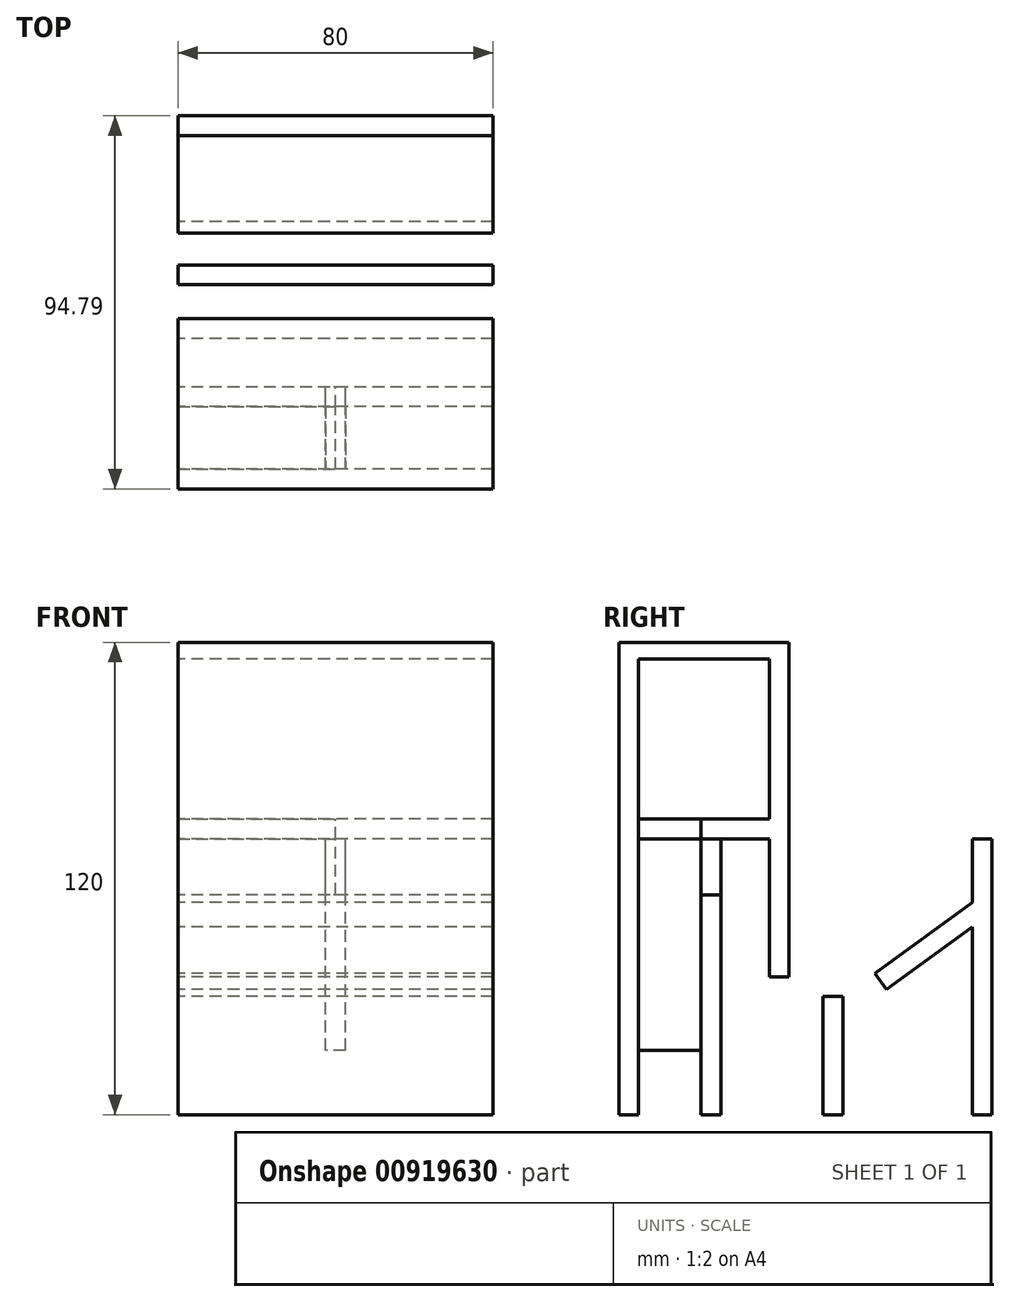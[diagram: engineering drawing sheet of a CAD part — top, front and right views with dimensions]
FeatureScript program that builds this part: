
annotation { "Feature Type Name" : "Feature", "Feature Type Description" : "" }
export const myFeature = defineFeature(function(context is Context, id is Id, definition is map)
    precondition{}
    {
        {
            var Q0;
            Q0=qCreatedBy(makeId("Right.planeOp"),FACE);
            var sketch = newSketch(context, id + "F0", { "sketchPlane" : qUnion([Q0])});
            skLineSegment(sketch, "E0.bottom", {"start": v(27.57, 0) * mm, "end": v(32.57, 0) * mm});
            skLineSegment(sketch, "E0.top", {"start": v(27.57, 30) * mm, "end": v(32.57, 30) * mm});
            skLineSegment(sketch, "E0.left", {"start": v(27.57, 0) * mm, "end": v(27.57, 30) * mm});
            skLineSegment(sketch, "E0.right", {"start": v(32.57, 0) * mm, "end": v(32.57, 30) * mm});
            skLineSegment(sketch, "E1", {"start": v(13.91, 35) * mm, "end": v(13.91, 70.09) * mm});
            skLineSegment(sketch, "E2", {"start": v(32.57, 30) * mm, "end": v(40.66, 35.88) * mm});
            skLineSegment(sketch, "E3", {"start": v(40.66, 35.88) * mm, "end": v(65.49, 53.92) * mm});
            skLineSegment(sketch, "E4", {"start": v(-19.3, 0) * mm, "end": v(-19.3, 70.09) * mm});
            skLineSegment(sketch, "E5", {"start": v(-19.3, 70.09) * mm, "end": v(13.91, 70.09) * mm});
            skLineSegment(sketch, "E6", {"start": v(32.57, 0) * mm, "end": v(65.49, 0) * mm});
            skLineSegment(sketch, "E7", {"start": v(65.49, 0) * mm, "end": v(65.49, 53.92) * mm});
            skLineSegment(sketch, "E8", {"start": v(-19.3, 70.09) * mm, "end": v(-19.3, 115.83) * mm});
            skLineSegment(sketch, "E9", {"start": v(-19.3, 115.83) * mm, "end": v(13.91, 115.83) * mm});
            skLineSegment(sketch, "E10.bottom", {"start": v(-19.3, 0) * mm, "end": v(-24.3, 0) * mm});
            skLineSegment(sketch, "E10.top", {"start": v(-19.3, 115.83) * mm, "end": v(-24.3, 115.83) * mm});
            skLineSegment(sketch, "E10.left", {"start": v(-19.3, 0) * mm, "end": v(-19.3, 115.83) * mm});
            skLineSegment(sketch, "E10.right", {"start": v(-24.3, 0) * mm, "end": v(-24.3, 115.83) * mm});
            skLineSegment(sketch, "E11.bottom", {"start": v(-24.3, 115.83) * mm, "end": v(13.91, 115.83) * mm});
            skLineSegment(sketch, "E11.top", {"start": v(-24.3, 120) * mm, "end": v(13.91, 120) * mm});
            skLineSegment(sketch, "E11.left", {"start": v(-24.3, 115.83) * mm, "end": v(-24.3, 120) * mm});
            skLineSegment(sketch, "E11.right", {"start": v(13.91, 115.83) * mm, "end": v(13.91, 120) * mm});
            skLineSegment(sketch, "E12.bottom", {"start": v(13.91, 120) * mm, "end": v(18.91, 120) * mm});
            skLineSegment(sketch, "E12.top", {"start": v(0, 70.09) * mm, "end": v(18.91, 70.09) * mm});
            skLineSegment(sketch, "E12.right", {"start": v(18.91, 120) * mm, "end": v(18.91, 70.09) * mm});
            skLineSegment(sketch, "E13", {"start": v(18.91, 70.09) * mm, "end": v(18.91, 35) * mm});
            skLineSegment(sketch, "E14", {"start": v(18.91, 35) * mm, "end": v(13.91, 35) * mm});
            skLineSegment(sketch, "E15", {"start": v(18.91, 35) * mm, "end": v(27.57, 30) * mm});
            skLineSegment(sketch, "E16", {"start": v(70.49, 53.94) * mm, "end": v(70.49, 0) * mm});
            skLineSegment(sketch, "E17", {"start": v(70.49, 0) * mm, "end": v(65.49, 0) * mm});
            skLineSegment(sketch, "E18", {"start": v(-19.3, 75.09) * mm, "end": v(13.91, 75.09) * mm});
            skLineSegment(sketch, "E19", {"start": v(13.91, 70.09) * mm, "end": v(13.91, 75.09) * mm});
            skLineSegment(sketch, "E20", {"start": v(13.91, 115.83) * mm, "end": v(13.91, 75.09) * mm});
            skLineSegment(sketch, "E21", {"start": v(40.66, 35.88) * mm, "end": v(43.6, 31.83) * mm});
            skLineSegment(sketch, "E22", {"start": v(43.6, 31.83) * mm, "end": v(65.49, 47.74) * mm});
            skLineSegment(sketch, "E23", {"start": v(-19.3, 0) * mm, "end": v(27.57, 0) * mm});
            skLineSegment(sketch, "E24", {"start": v(-3.45, 0) * mm, "end": v(-3.45, 55.88) * mm});
            skLineSegment(sketch, "E25", {"start": v(-3.45, 55.88) * mm, "end": v(1.55, 55.88) * mm});
            skLineSegment(sketch, "E26", {"start": v(1.55, 55.88) * mm, "end": v(1.55, 0) * mm});
            skLineSegment(sketch, "E27", {"start": v(65.49, 70.09) * mm, "end": v(65.49, 53.92) * mm});
            skLineSegment(sketch, "E28", {"start": v(65.49, 70.09) * mm, "end": v(70.49, 70.09) * mm});
            skLineSegment(sketch, "E29", {"start": v(70.49, 70.09) * mm, "end": v(70.49, 53.94) * mm});
            skLineSegment(sketch, "E30", {"start": v(-3.45, 55.88) * mm, "end": v(-3.45, 70.09) * mm});
            skLineSegment(sketch, "E31", {"start": v(1.55, 55.88) * mm, "end": v(1.55, 70.09) * mm});
            skLineSegment(sketch, "E32", {"start": v(-3.45, 70.09) * mm, "end": v(-3.45, 75.09) * mm});
            skLineSegment(sketch, "E33", {"start": v(-3.45, 16.34) * mm, "end": v(-19.3, 16.34) * mm});
            skSolve(sketch);
        }
        {
            var Q0;
            Q0=makeQuery(id+"F0.imprint","IMPRINT",FACE,{"disambiguationData":[TD([[makeQuery(id+"F0.imprint","IMPRINT",EDGE,{"derivedFrom":sQuery(id+"F0.wireOp",EDGE,"E11.top")}),-1.0]])]});
            var Q1;
            {var subQ5=sQuery(id+"F0.wireOp",EDGE,"E10.bottom");Q1=makeQuery(id+"F0.imprint","IMPRINT",FACE,{"disambiguationData":[TD([[makeQuery(id+"F0.imprint","IMPRINT",EDGE,{"derivedFrom":subQ5}),-1.0]])]});}
            var Q2;
            Q2=makeQuery(id+"F0.imprint","IMPRINT",FACE,{"disambiguationData":[TD([[makeQuery(id+"F0.imprint","IMPRINT",EDGE,{"derivedFrom":sQuery(id+"F0.wireOp",EDGE,"E11.right")}),-1.0]])]});
            var Q3;
            {var subQ0=sQuery(id+"F0.wireOp",EDGE,"E1");Q3=makeQuery(id+"F0.imprint","IMPRINT",FACE,{"disambiguationData":[TD([[makeQuery(id+"F0.imprint","IMPRINT",EDGE,{"derivedFrom":subQ0}),-1.0]])]});}
            var Q4;
            Q4=makeQuery(id+"F0.imprint","IMPRINT",FACE,{"disambiguationData":[TD([[makeQuery(id+"F0.imprint","IMPRINT",EDGE,{"derivedFrom":sQuery(id+"F0.wireOp",EDGE,"Fx7D5mdC-qbW7-CEck-KvEF-XUMli4D04gyy")}),1.0]])]});
            var Q5;
            Q5=makeQuery(id+"F0.imprint","IMPRINT",FACE,{"disambiguationData":[TD([[makeQuery(id+"F0.imprint","IMPRINT",EDGE,{"derivedFrom":sQuery(id+"F0.wireOp",EDGE,"E0.bottom")}),1.0]])]});
            var Q6;
            {var subQ0=sQuery(id+"F0.wireOp",EDGE,"E3");Q6=makeQuery(id+"F0.imprint","IMPRINT",FACE,{"disambiguationData":[TD([[makeQuery(id+"F0.imprint","IMPRINT",EDGE,{"derivedFrom":subQ0}),-1.0]])]});}
            var Q7;
            {var subQ0=sQuery(id+"F0.wireOp",EDGE,"xSf1LqSM-Zb7q-qxLd-u2kb-gej299T4ug9K");Q7=makeQuery(id+"F0.imprint","IMPRINT",FACE,{"disambiguationData":[TD([[makeQuery(id+"F0.imprint","IMPRINT",EDGE,{"derivedFrom":subQ0}),-1.0]])]});}
            var Q8;
            {var subQ0=sQuery(id+"F0.wireOp",EDGE,"E24");Q8=makeQuery(id+"F0.imprint","IMPRINT",FACE,{"disambiguationData":[TD([[makeQuery(id+"F0.imprint","IMPRINT",EDGE,{"derivedFrom":subQ0}),-1.0]])]});}
            var Q9;
            Q9=makeQuery(id+"F0.imprint","IMPRINT",FACE,{"disambiguationData":[TD([[makeQuery(id+"F0.imprint","IMPRINT",EDGE,{"derivedFrom":sQuery(id+"F0.wireOp",EDGE,"E16")}),-1.0]])]});
            var Q10;
            {var subQ0=sQuery(id+"F0.wireOp",EDGE,"E19");Q10=makeQuery(id+"F0.imprint","IMPRINT",FACE,{"disambiguationData":[TD([[makeQuery(id+"F0.imprint","IMPRINT",EDGE,{"derivedFrom":subQ0}),1.0]])]});}
            extrude(context, id + "F1", {"entities" : qUnion([Q0, Q1, Q2, Q3, Q4, Q5, Q6, Q7, Q8, Q9, Q10]), "endBound" : BoundingType.SYMMETRIC, "depth" : 80 * mm, "offsetDistance" : 25 * mm});
        }
        {
            var Q0;
            Q0=makeQuery(id+"F0.imprint","IMPRINT",FACE,{"disambiguationData":[TD([[makeQuery(id+"F0.imprint","IMPRINT",EDGE,{"derivedFrom":sQuery(id+"F0.wireOp",EDGE,"E25")}),1.0]])]});
            var Q1;
            {var subQ0=sQuery(id+"F0.wireOp",EDGE,"E30");Q1=makeQuery(id+"F0.imprint","IMPRINT",FACE,{"disambiguationData":[TD([[makeQuery(id+"F0.imprint","IMPRINT",EDGE,{"derivedFrom":subQ0}),1.0]])]});}
            extrude(context, id + "F2", {"entities" : qUnion([Q0, Q1]), "endBound" : BoundingType.SYMMETRIC, "depth" : 5 * mm, "offsetDistance" : 25 * mm});
        }
        {
            var Q0;
            Q0=makeQuery(id+"F0.imprint","IMPRINT",FACE,{"disambiguationData":[TD([[makeQuery(id+"F0.imprint","IMPRINT",EDGE,{"derivedFrom":sQuery(id+"F0.wireOp",EDGE,"E25")}),1.0]])]});
            var Q1;
            Q1=makeQuery(id+"F1.opExtrude","CAP_FACE",FACE,{"disambiguationData":[OSD([sQuery(id+"F0.wireOp",EDGE,"E1"),sQuery(id+"F0.wireOp",EDGE,"E5"),sQuery(id+"F0.wireOp",EDGE,"E10.bottom"),sQuery(id+"F0.wireOp",EDGE,"E10.left"),sQuery(id+"F0.wireOp",EDGE,"E10.right"),sQuery(id+"F0.wireOp",EDGE,"E11.bottom"),sQuery(id+"F0.wireOp",EDGE,"E11.top"),sQuery(id+"F0.wireOp",EDGE,"E11.left"),sQuery(id+"F0.wireOp",EDGE,"E12.bottom"),sQuery(id+"F0.wireOp",EDGE,"E12.top"),sQuery(id+"F0.wireOp",EDGE,"E12.right"),sQuery(id+"F0.wireOp",EDGE,"E13"),sQuery(id+"F0.wireOp",EDGE,"E14"),sQuery(id+"F0.wireOp",EDGE,"E18"),sQuery(id+"F0.wireOp",EDGE,"E20"),sQuery(id+"F0.wireOp",EDGE,"E32")])],"isStart":false});
            extrude(context, id + "F3", {"entities" : qUnion([Q0]), "endBound" : BoundingType.UP_TO_SURFACE, "depth" : 25 * mm, "endBoundEntityFace" : qUnion([Q1]), "offsetDistance" : 25 * mm});
        }
        {
            var Q0;
            {var subQ3=sQuery(id+"F0.wireOp",EDGE,"E32");Q0=makeQuery(id+"F0.imprint","IMPRINT",FACE,{"disambiguationData":[TD([[makeQuery(id+"F0.imprint","IMPRINT",EDGE,{"derivedFrom":subQ3}),1.0]])]});}
            var Q1;
            Q1=makeQuery(id+"F1.opExtrude","CAP_FACE",FACE,{"disambiguationData":[OSD([sQuery(id+"F0.wireOp",EDGE,"E1"),sQuery(id+"F0.wireOp",EDGE,"E5"),sQuery(id+"F0.wireOp",EDGE,"E10.bottom"),sQuery(id+"F0.wireOp",EDGE,"E10.left"),sQuery(id+"F0.wireOp",EDGE,"E10.right"),sQuery(id+"F0.wireOp",EDGE,"E11.bottom"),sQuery(id+"F0.wireOp",EDGE,"E11.top"),sQuery(id+"F0.wireOp",EDGE,"E11.left"),sQuery(id+"F0.wireOp",EDGE,"E12.bottom"),sQuery(id+"F0.wireOp",EDGE,"E12.top"),sQuery(id+"F0.wireOp",EDGE,"E12.right"),sQuery(id+"F0.wireOp",EDGE,"E13"),sQuery(id+"F0.wireOp",EDGE,"E14"),sQuery(id+"F0.wireOp",EDGE,"E18"),sQuery(id+"F0.wireOp",EDGE,"E20"),sQuery(id+"F0.wireOp",EDGE,"E32")])],"isStart":true});
            extrude(context, id + "F4", {"entities" : qUnion([Q0]), "endBound" : BoundingType.UP_TO_SURFACE, "oppositeDirection" : true, "depth" : 25 * mm, "endBoundEntityFace" : qUnion([Q1]), "offsetDistance" : 25 * mm});
        }
    });
